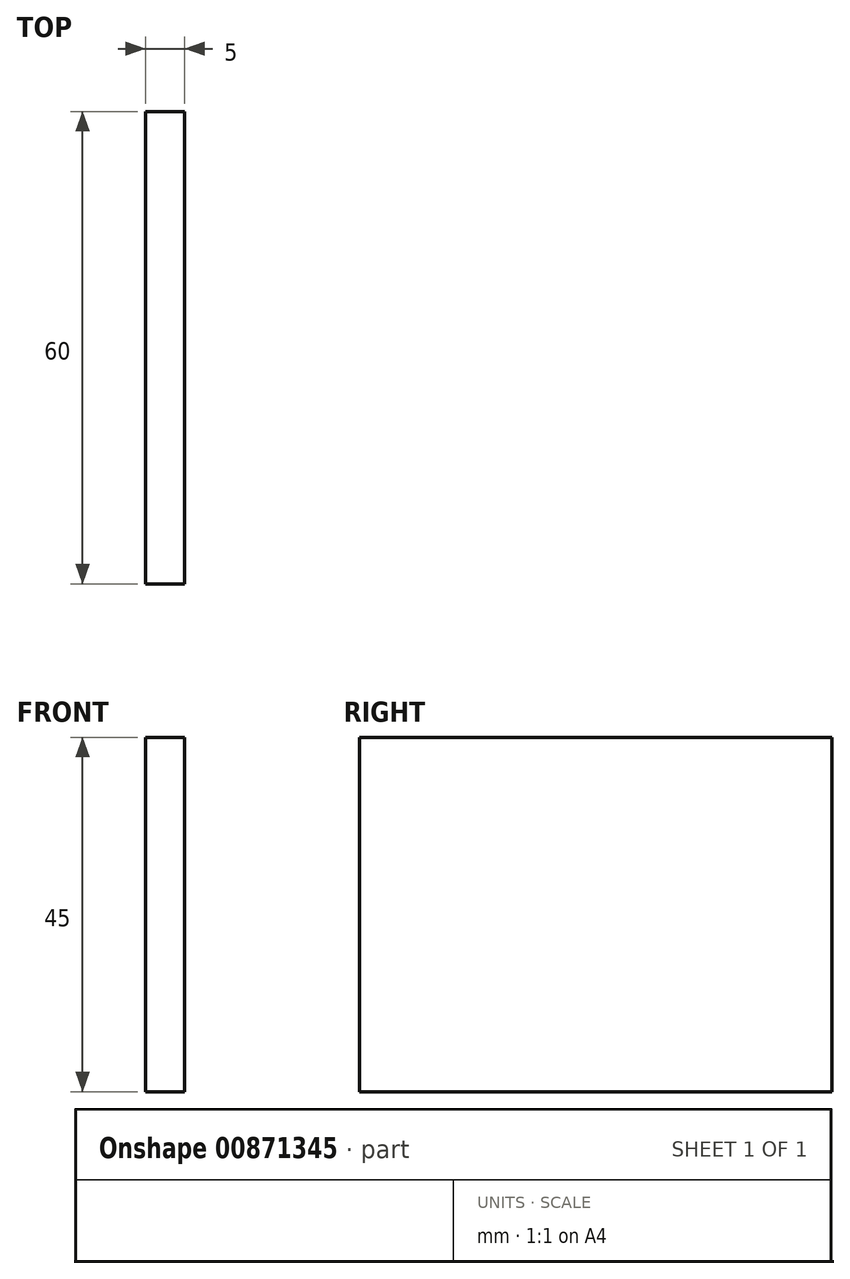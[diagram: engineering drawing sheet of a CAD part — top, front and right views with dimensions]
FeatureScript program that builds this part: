
annotation { "Feature Type Name" : "Feature", "Feature Type Description" : "" }
export const myFeature = defineFeature(function(context is Context, id is Id, definition is map)
    precondition{}
    {
        {
            var Q0;
            Q0=qCreatedBy(makeId("Front.planeOp"),FACE);
            var sketch = newSketch(context, id + "F0", { "sketchPlane" : qUnion([Q0])});
            skLineSegment(sketch, "E0.bottom", {"start": v(-12.76, 18.7) * mm, "end": v(-7.76, 18.7) * mm});
            skLineSegment(sketch, "E0.top", {"start": v(-12.76, -26.3) * mm, "end": v(-7.76, -26.3) * mm});
            skLineSegment(sketch, "E0.left", {"start": v(-12.76, 18.7) * mm, "end": v(-12.76, -26.3) * mm});
            skLineSegment(sketch, "E0.right", {"start": v(-7.76, 18.7) * mm, "end": v(-7.76, -26.3) * mm});
            skSolve(sketch);
        }
        {
            var Q0;
            Q0 = qSketchRegion(id + "F0", true);
            extrude(context, id + "F1", {"entities" : qUnion([Q0]), "depth" : 60 * mm, "offsetDistance" : 25 * mm});
        }
    });
